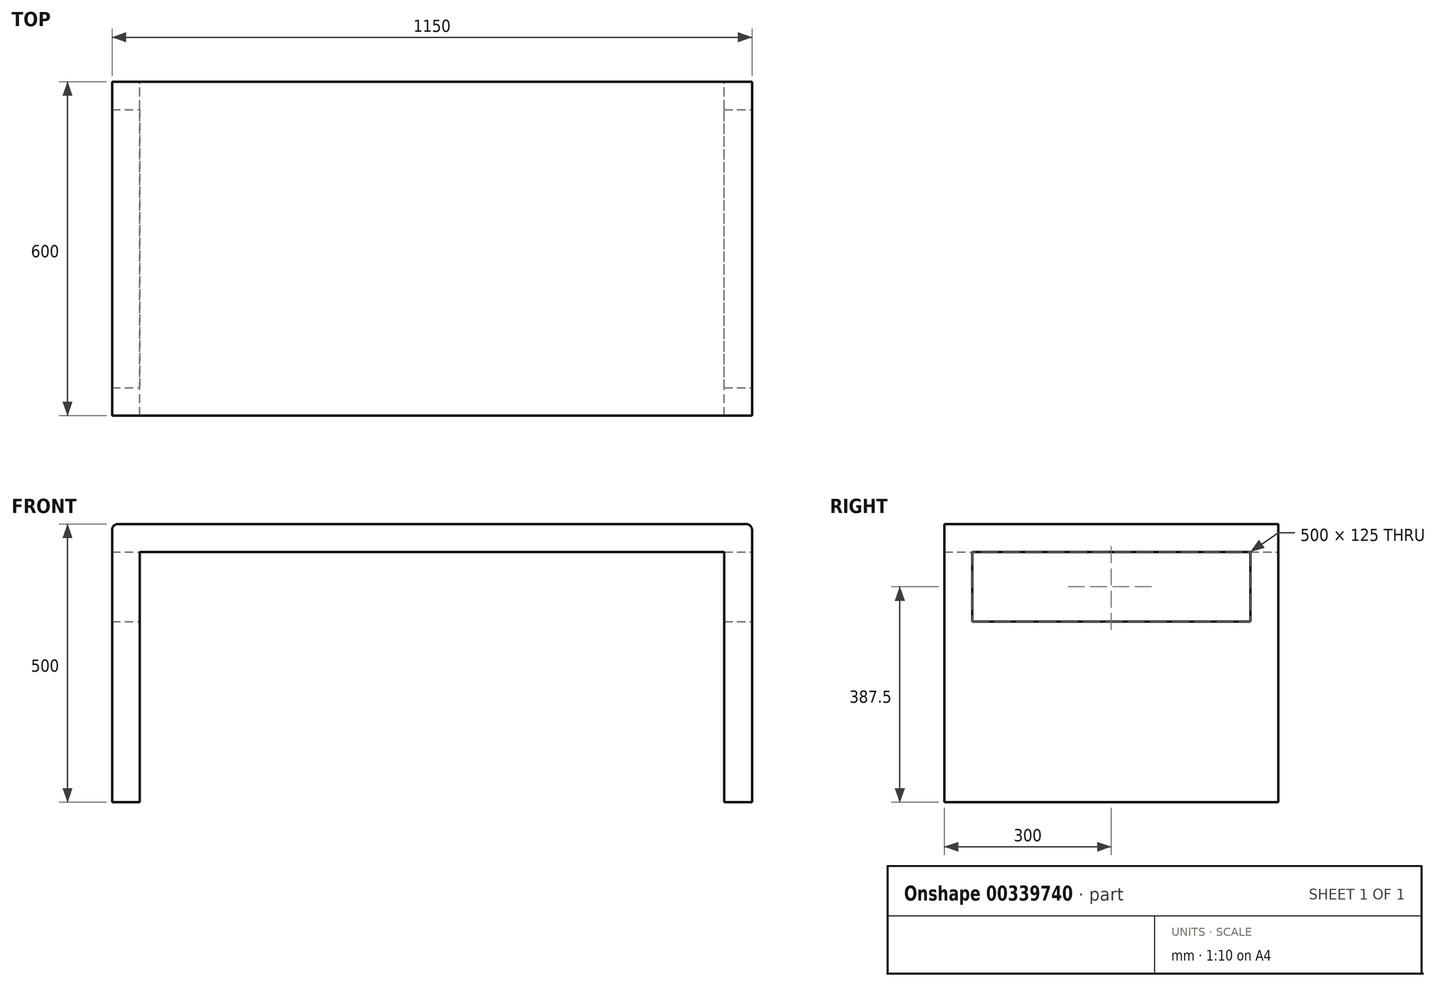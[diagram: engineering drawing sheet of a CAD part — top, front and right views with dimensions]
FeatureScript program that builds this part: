
annotation { "Feature Type Name" : "Feature", "Feature Type Description" : "" }
export const myFeature = defineFeature(function(context is Context, id is Id, definition is map)
    precondition{}
    {
        {
            var Q0;
            Q0=qCreatedBy(makeId("Top.planeOp"),FACE);
            var sketch = newSketch(context, id + "F0", { "sketchPlane" : qUnion([Q0])});
            skLineSegment(sketch, "E0.bottom", {"start": v(0, 0) * mm, "end": v(575, 0) * mm});
            skLineSegment(sketch, "E0.top", {"start": v(0, -300) * mm, "end": v(575, -300) * mm});
            skLineSegment(sketch, "E0.left", {"start": v(0, 0) * mm, "end": v(0, -300) * mm});
            skLineSegment(sketch, "E0.right", {"start": v(575, 0) * mm, "end": v(575, -300) * mm});
            skSolve(sketch);
        }
        {
            var Q0;
            Q0=makeQuery(id+"F0.imprint","IMPRINT",FACE,{"disambiguationData":[TD([[makeQuery(id+"F0.imprint","IMPRINT",EDGE,{"derivedFrom":sQuery(id+"F0.wireOp",EDGE,"E0.bottom")}),-1.0]])]});
            extrude(context, id + "F1", {"entities" : qUnion([Q0]), "oppositeDirection" : true, "depth" : 50 * mm});
        }
        {
            var Q0;
            Q0=makeQuery(id+"F1.opExtrude","CAP_FACE",FACE,{"disambiguationData":[OSD([sQuery(id+"F0.wireOp",EDGE,"E0.bottom"),sQuery(id+"F0.wireOp",EDGE,"E0.top"),sQuery(id+"F0.wireOp",EDGE,"E0.left"),sQuery(id+"F0.wireOp",EDGE,"E0.right")])],"isStart":false});
            var sketch = newSketch(context, id + "F2", { "sketchPlane" : qUnion([Q0])});
            skLineSegment(sketch, "E1.bottom", {"start": v(575, 300) * mm, "end": v(525, 300) * mm});
            skLineSegment(sketch, "E1.top", {"start": v(575, 0) * mm, "end": v(525, 0) * mm});
            skLineSegment(sketch, "E1.left", {"start": v(575, 300) * mm, "end": v(575, 0) * mm});
            skLineSegment(sketch, "E1.right", {"start": v(525, 300) * mm, "end": v(525, 0) * mm});
            skSolve(sketch);
        }
        {
            var Q0;
            Q0=qSketchRegion(id+"F2",true);
            extrude(context, id + "F3", {"entities" : qUnion([Q0]), "operationType" : NewBodyOperationType.ADD, "depth" : 450 * mm});
        }
        {
            var Q0;
            Q0=makeQuery(id+"F3.boolean.opBoolean","MERGE",FACE,{"derivedFrom":[makeQuery(id+"F1.opExtrude","SWEPT_FACE",FACE,{"disambiguationData":[OSD([sQuery(id+"F0.wireOp",EDGE,"E0.right")])]}),makeQuery(id+"F3.opExtrude","SWEPT_FACE",FACE,{"disambiguationData":[OSD([sQuery(id+"F2.wireOp",EDGE,"E1.left")])]})]});
            var sketch = newSketch(context, id + "F4", { "sketchPlane" : qUnion([Q0])});
            skLineSegment(sketch, "E2", {"start": v(0, -80) * mm, "end": v(50, -30) * mm});
            skLineSegment(sketch, "E3", {"start": v(50, -30) * mm, "end": v(120.71, -30) * mm});
            skLineSegment(sketch, "E4", {"start": v(120.71, -30) * mm, "end": v(0, -150.71) * mm});
            skLineSegment(sketch, "E5", {"start": v(0, -150.71) * mm, "end": v(0, -80) * mm});
            skSolve(sketch);
        }
        {
            var Q0;
            Q0=makeQuery(id+"F4.imprint","IMPRINT",FACE,{"disambiguationData":[TD([[makeQuery(id+"F4.imprint","IMPRINT",EDGE,{"derivedFrom":sQuery(id+"F4.wireOp",EDGE,"E2")}),-1.0]])]});
            var Q1;
            {var subQ1=sQuery(id+"F2.wireOp",EDGE,"E1.right");var subQ3=sQuery(id+"F0NKJpxBL8xCCbG_1.wireOp",EDGE,"L7aNiJfJ-wDWt-VzWT-kvhX-rd4orgkB66cD");Q1=makeQuery(id+"Fv87nby8ifMDPul_1.boolean.opBoolean","SPLIT",FACE,{"disambiguationData":[TD([makeQuery(id+"Fv87nby8ifMDPul_1.opExtrude","SWEPT_FACE",FACE,{"disambiguationData":[OSD([subQ3])]})])],"derivedFrom":makeQuery(id+"F3.opExtrude","SWEPT_FACE",FACE,{"disambiguationData":[OSD([subQ1])]})});}
            extrude(context, id + "F5", {"entities" : qUnion([Q0]), "operationType" : NewBodyOperationType.ADD, "endBound" : BoundingType.UP_TO_SURFACE, "oppositeDirection" : true, "endBoundEntityFace" : qUnion([Q1]), "depth" : 25 * mm});
        }
        {
            var Q0;
            Q0=makeQuery(id+"F1.opExtrude","SWEPT_BODY",BODY,{"disambiguationData":[OSD([sQuery(id+"F0.wireOp",EDGE,"E0.bottom"),sQuery(id+"F0.wireOp",EDGE,"E0.top"),sQuery(id+"F0.wireOp",EDGE,"E0.left"),sQuery(id+"F0.wireOp",EDGE,"E0.right")])]});
            var Q1;
            Q1=qCreatedBy(makeId("Right.planeOp"),FACE);
            mirror(context, id + "F6", {"operationType" : NewBodyOperationType.ADD, "entities" : qUnion([Q0]), "mirrorPlane" : qUnion([Q1])});
        }
        {
            var Q0;
            Q0=makeQuery(id+"F1.opExtrude","SWEPT_BODY",BODY,{"disambiguationData":[OSD([sQuery(id+"F0.wireOp",EDGE,"E0.bottom"),sQuery(id+"F0.wireOp",EDGE,"E0.top"),sQuery(id+"F0.wireOp",EDGE,"E0.left"),sQuery(id+"F0.wireOp",EDGE,"E0.right")])]});
            var Q1;
            Q1=qCreatedBy(makeId("Front.planeOp"),FACE);
            mirror(context, id + "F7", {"operationType" : NewBodyOperationType.ADD, "entities" : qUnion([Q0]), "mirrorPlane" : qUnion([Q1])});
        }
        {
            var Q0;
            {var subQ0=makeQuery(id+"F5.boolean.opBoolean","MERGE",FACE,{"derivedFrom":[makeQuery(id+"F3.boolean.opBoolean","MERGE",FACE,{"derivedFrom":[makeQuery(id+"F1.opExtrude","SWEPT_FACE",FACE,{"disambiguationData":[OSD([sQuery(id+"F0.wireOp",EDGE,"E0.right")])]}),makeQuery(id+"F3.opExtrude","SWEPT_FACE",FACE,{"disambiguationData":[OSD([sQuery(id+"F2.wireOp",EDGE,"E1.left")])]})]}),makeQuery(id+"F5.opExtrude","CAP_FACE",FACE,{"disambiguationData":[OSD([sQuery(id+"F4.wireOp",EDGE,"E2"),sQuery(id+"F4.wireOp",EDGE,"E3"),sQuery(id+"F4.wireOp",EDGE,"E4"),sQuery(id+"F4.wireOp",EDGE,"E5")])],"isStart":true})]});Q0=makeQuery(id+"F7.boolean.opBoolean","MERGE",FACE,{"derivedFrom":[subQ0,makeQuery(id+"F7.opPattern","COPY",FACE,{"derivedFrom":subQ0,"instanceName":"1"})]});}
            var sketch = newSketch(context, id + "F8", { "sketchPlane" : qUnion([Q0])});
            skLineSegment(sketch, "E6.bottom", {"start": v(-250, -50) * mm, "end": v(250, -50) * mm});
            skLineSegment(sketch, "E6.top", {"start": v(-250, -175) * mm, "end": v(250, -175) * mm});
            skLineSegment(sketch, "E6.left", {"start": v(-250, -50) * mm, "end": v(-250, -175) * mm});
            skLineSegment(sketch, "E6.right", {"start": v(250, -50) * mm, "end": v(250, -175) * mm});
            skSolve(sketch);
        }
        {
            var Q0;
            Q0=makeQuery(id+"F8.imprint","IMPRINT",FACE,{"disambiguationData":[TD([[makeQuery(id+"F8.imprint","IMPRINT",EDGE,{"derivedFrom":sQuery(id+"F8.wireOp",EDGE,"E6.bottom")}),-1.0]])]});
            extrude(context, id + "F9", {"entities" : qUnion([Q0]), "operationType" : NewBodyOperationType.REMOVE, "endBound" : BoundingType.THROUGH_ALL, "oppositeDirection" : true, "depth" : 50 * mm});
        }
        {
            var Q0;
            {var subQ0=makeQuery(id+"F1.opExtrude","CAP_EDGE",EDGE,{"disambiguationData":[OSD([sQuery(id+"F0.wireOp",EDGE,"E0.right")])],"isStart":true});Q0=makeQuery(id+"F7.boolean.opBoolean","MERGE",EDGE,{"derivedFrom":[subQ0,makeQuery(id+"F7.opPattern","COPY",EDGE,{"derivedFrom":subQ0,"instanceName":"1"})]});}
            var Q1;
            {var subQ0=makeQuery(id+"F6.opPattern","COPY",EDGE,{"derivedFrom":makeQuery(id+"F1.opExtrude","CAP_EDGE",EDGE,{"disambiguationData":[OSD([sQuery(id+"F0.wireOp",EDGE,"E0.right")])],"isStart":true}),"instanceName":"1"});Q1=makeQuery(id+"F7.boolean.opBoolean","MERGE",EDGE,{"derivedFrom":[subQ0,makeQuery(id+"F7.opPattern","COPY",EDGE,{"derivedFrom":subQ0,"instanceName":"1"})]});}
            fillet(context, id + "F10", {"entities" : qUnion([Q0, Q1]), "radius" : 10 * mm, "tangentPropagation" : true, "allowEdgeOverflow" : false});
        }
    });
